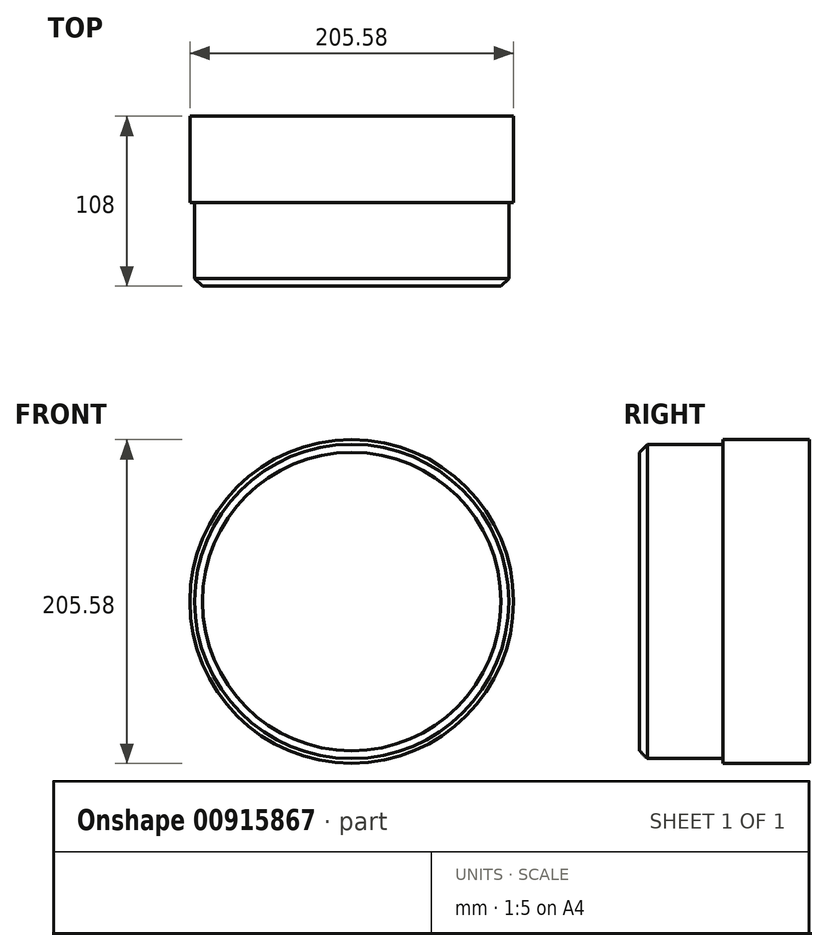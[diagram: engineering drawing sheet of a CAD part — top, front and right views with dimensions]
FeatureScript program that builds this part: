
annotation { "Feature Type Name" : "Feature", "Feature Type Description" : "" }
export const myFeature = defineFeature(function(context is Context, id is Id, definition is map)
    precondition{}
    {
        {
            var Q0;
            Q0=qCreatedBy(makeId("Front.planeOp"),FACE);
            var sketch = newSketch(context, id + "F0", { "sketchPlane" : qUnion([Q0])});
            skCircle(sketch, "E0", {"center": v(0, 0) * mm, "radius": 102.78 * mm});
            skCircle(sketch, "E1", {"center": v(0, 0) * mm, "radius": 99.8 * mm});
            skSolve(sketch);
        }
        {
            var Q0;
            Q0=makeQuery(id+"F0.imprint","IMPRINT",FACE,{"disambiguationData":[TD([[makeQuery(id+"F0.imprint","IMPRINT",EDGE,{"derivedFrom":sQuery(id+"F0.wireOp",EDGE,"E0")}),1.0]])]});
            extrude(context, id + "F1", {"entities" : qUnion([Q0]), "depth" : 55 * mm, "offsetDistance" : 25 * mm});
        }
        {
            var Q0;
            Q0=makeQuery(id+"F0.imprint","IMPRINT",FACE,{"disambiguationData":[TD([[makeQuery(id+"F0.imprint","IMPRINT",EDGE,{"derivedFrom":sQuery(id+"F0.wireOp",EDGE,"E1")}),1.0]])]});
            extrude(context, id + "F2", {"entities" : qUnion([Q0]), "operationType" : NewBodyOperationType.ADD, "depth" : 108 * mm, "offsetDistance" : 25 * mm});
        }
        {
            var Q0;
            Q0=makeQuery(id+"F2.opExtrude","CAP_EDGE",EDGE,{"disambiguationData":[OSD([sQuery(id+"F0.wireOp",EDGE,"E1")])],"isStart":false});
            chamfer(context, id + "F3", {"entities" : qUnion([Q0]), "width" : 5 * mm, "tangentPropagation" : true});
        }
    });
